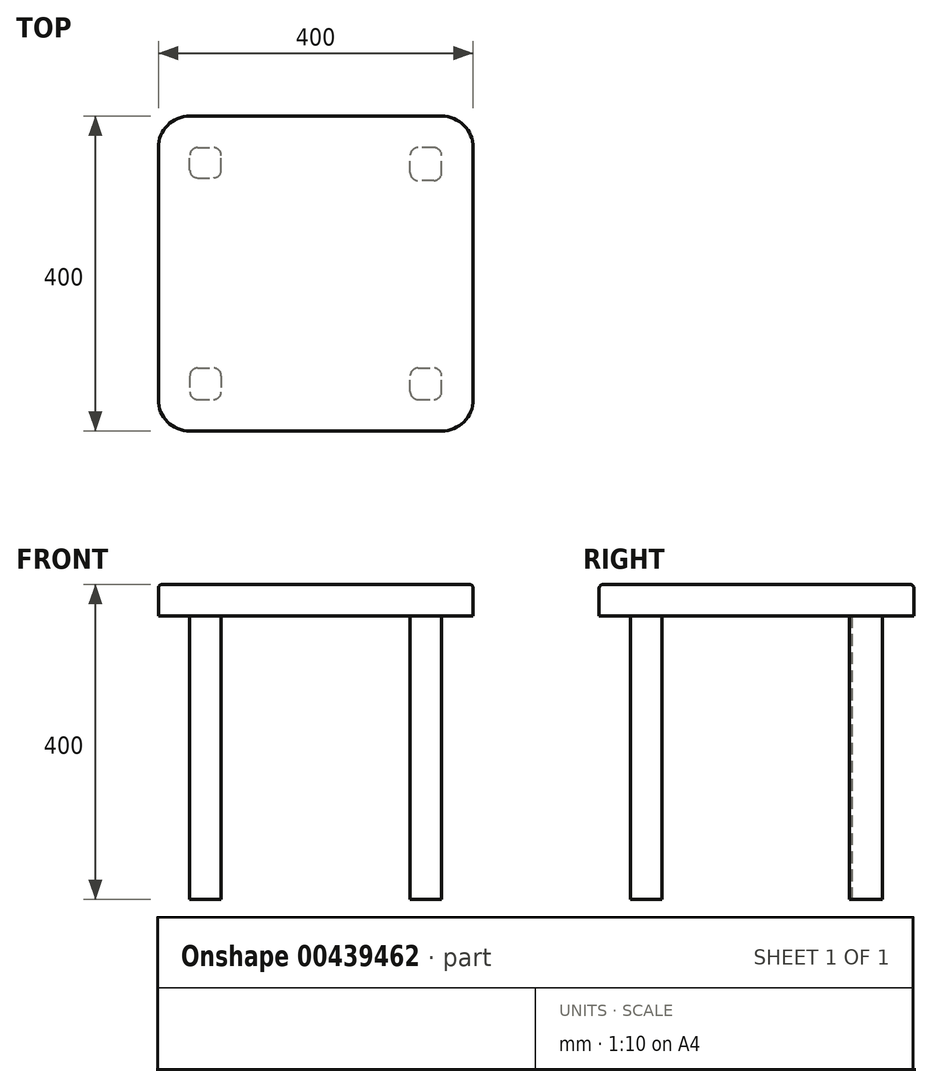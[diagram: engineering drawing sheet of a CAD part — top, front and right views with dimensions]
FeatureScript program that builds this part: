
annotation { "Feature Type Name" : "Feature", "Feature Type Description" : "" }
export const myFeature = defineFeature(function(context is Context, id is Id, definition is map)
    precondition{}
    {
        {
            var Q0;
            Q0=qCreatedBy(makeId("Top.planeOp"),FACE);
            var sketch = newSketch(context, id + "F0", { "sketchPlane" : qUnion([Q0])});
            skLineSegment(sketch, "E0.bottom", {"start": v(-145.08, 267.03) * mm, "end": v(174.92, 267.03) * mm});
            skLineSegment(sketch, "E0.top", {"start": v(-145.08, -132.97) * mm, "end": v(174.92, -132.97) * mm});
            skLineSegment(sketch, "E0.left", {"start": v(-185.08, 227.03) * mm, "end": v(-185.08, -92.97) * mm});
            skLineSegment(sketch, "E0.right", {"start": v(214.92, 227.03) * mm, "end": v(214.92, -92.97) * mm});
            skPoint(sketch, "E1.visualSharp", {"position": v(-185.08, 267.03) * mm});
            skArc(sketch, "E1.filletArc", {"start": v(-145.08, 267.03) * mm, "mid": v(-173.36, 255.31) * mm, "end": v(-185.08, 227.03) * mm});
            skPoint(sketch, "E2.visualSharp", {"position": v(-185.08, -132.97) * mm});
            skArc(sketch, "E2.filletArc", {"start": v(-185.08, -92.97) * mm, "mid": v(-173.36, -121.26) * mm, "end": v(-145.08, -132.97) * mm});
            skPoint(sketch, "E3.visualSharp", {"position": v(214.92, -132.97) * mm});
            skArc(sketch, "E3.filletArc", {"start": v(174.92, -132.97) * mm, "mid": v(203.2, -121.26) * mm, "end": v(214.92, -92.97) * mm});
            skPoint(sketch, "E4.visualSharp", {"position": v(214.92, 267.03) * mm});
            skArc(sketch, "E4.filletArc", {"start": v(214.92, 227.03) * mm, "mid": v(203.2, 255.31) * mm, "end": v(174.92, 267.03) * mm});
            skSolve(sketch);
        }
        {
            var Q0;
            Q0 = qSketchRegion(id + "F0", true);
            extrude(context, id + "F1", {"entities" : qUnion([Q0]), "depth" : 40 * mm});
        }
        {
            var Q0;
            Q0=makeQuery(id+"F1.opExtrude","CAP_FACE",FACE,{"disambiguationData":[OSD([sQuery(id+"F0.wireOp",EDGE,"E0.bottom"),sQuery(id+"F0.wireOp",EDGE,"E0.top"),sQuery(id+"F0.wireOp",EDGE,"E0.left"),sQuery(id+"F0.wireOp",EDGE,"E0.right"),sQuery(id+"F0.wireOp",EDGE,"E1.filletArc"),sQuery(id+"F0.wireOp",EDGE,"E2.filletArc"),sQuery(id+"F0.wireOp",EDGE,"E3.filletArc"),sQuery(id+"F0.wireOp",EDGE,"E4.filletArc")])],"isStart":true});
            var sketch = newSketch(context, id + "F2", { "sketchPlane" : qUnion([Q0])});
            skLineSegment(sketch, "E5.bottom", {"start": v(-135.08, 52.97) * mm, "end": v(-115.08, 52.97) * mm});
            skLineSegment(sketch, "E5.top", {"start": v(-135.08, 92.97) * mm, "end": v(-115.08, 92.97) * mm});
            skLineSegment(sketch, "E5.left", {"start": v(-145.08, 62.97) * mm, "end": v(-145.08, 82.97) * mm});
            skLineSegment(sketch, "E5.right", {"start": v(-105.08, 62.97) * mm, "end": v(-105.08, 82.97) * mm});
            skPoint(sketch, "E6.visualSharp", {"position": v(-145.08, 92.97) * mm});
            skArc(sketch, "E6.filletArc", {"start": v(-135.08, 92.97) * mm, "mid": v(-142.15, 90.04) * mm, "end": v(-145.08, 82.97) * mm});
            skPoint(sketch, "E7.visualSharp", {"position": v(-105.08, 92.97) * mm});
            skArc(sketch, "E7.filletArc", {"start": v(-105.08, 82.97) * mm, "mid": v(-108, 90.04) * mm, "end": v(-115.08, 92.97) * mm});
            skPoint(sketch, "E8.visualSharp", {"position": v(-105.08, 52.97) * mm});
            skArc(sketch, "E8.filletArc", {"start": v(-115.08, 52.97) * mm, "mid": v(-108, 55.9) * mm, "end": v(-105.08, 62.97) * mm});
            skPoint(sketch, "E9.visualSharp", {"position": v(-145.08, 52.97) * mm});
            skArc(sketch, "E9.filletArc", {"start": v(-145.08, 62.97) * mm, "mid": v(-142.15, 55.9) * mm, "end": v(-135.08, 52.97) * mm});
            skLineSegment(sketch, "E10.bottom", {"start": v(-135.08, -188.62) * mm, "end": v(-115.08, -188.62) * mm});
            skLineSegment(sketch, "E10.top", {"start": v(-135.08, -227.03) * mm, "end": v(-115.08, -227.03) * mm});
            skLineSegment(sketch, "E10.left", {"start": v(-145.08, -198.62) * mm, "end": v(-145.08, -217.03) * mm});
            skLineSegment(sketch, "E10.right", {"start": v(-105.08, -198.62) * mm, "end": v(-105.08, -217.03) * mm});
            skLineSegment(sketch, "E11.bottom", {"start": v(164.92, -185.22) * mm, "end": v(144.92, -185.22) * mm});
            skLineSegment(sketch, "E11.top", {"start": v(164.92, -227.03) * mm, "end": v(144.92, -227.03) * mm});
            skLineSegment(sketch, "E11.left", {"start": v(174.92, -195.22) * mm, "end": v(174.92, -217.03) * mm});
            skLineSegment(sketch, "E11.right", {"start": v(134.92, -195.22) * mm, "end": v(134.92, -217.03) * mm});
            skLineSegment(sketch, "E12.bottom", {"start": v(144.92, 92.97) * mm, "end": v(164.92, 92.97) * mm});
            skLineSegment(sketch, "E12.top", {"start": v(144.92, 53.04) * mm, "end": v(164.92, 53.04) * mm});
            skLineSegment(sketch, "E12.left", {"start": v(134.92, 82.97) * mm, "end": v(134.92, 63.04) * mm});
            skLineSegment(sketch, "E12.right", {"start": v(174.92, 82.97) * mm, "end": v(174.92, 63.04) * mm});
            skPoint(sketch, "E13.visualSharp", {"position": v(-105.08, -188.62) * mm});
            skArc(sketch, "E13.filletArc", {"start": v(-105.08, -198.62) * mm, "mid": v(-108, -191.55) * mm, "end": v(-115.08, -188.62) * mm});
            skPoint(sketch, "E14.visualSharp", {"position": v(-105.08, -227.03) * mm});
            skArc(sketch, "E14.filletArc", {"start": v(-115.08, -227.03) * mm, "mid": v(-108, -224.1) * mm, "end": v(-105.08, -217.03) * mm});
            skPoint(sketch, "E15.visualSharp", {"position": v(-145.08, -227.03) * mm});
            skArc(sketch, "E15.filletArc", {"start": v(-145.08, -217.03) * mm, "mid": v(-142.15, -224.1) * mm, "end": v(-135.08, -227.03) * mm});
            skPoint(sketch, "E16.visualSharp", {"position": v(-145.08, -188.62) * mm});
            skArc(sketch, "E16.filletArc", {"start": v(-135.08, -188.62) * mm, "mid": v(-142.15, -191.55) * mm, "end": v(-145.08, -198.62) * mm});
            skPoint(sketch, "E17.visualSharp", {"position": v(134.92, -185.22) * mm});
            skArc(sketch, "E17.filletArc", {"start": v(144.92, -185.22) * mm, "mid": v(137.85, -188.15) * mm, "end": v(134.92, -195.22) * mm});
            skPoint(sketch, "E18.visualSharp", {"position": v(174.92, -185.22) * mm});
            skArc(sketch, "E18.filletArc", {"start": v(174.92, -195.22) * mm, "mid": v(172, -188.15) * mm, "end": v(164.92, -185.22) * mm});
            skPoint(sketch, "E19.visualSharp", {"position": v(134.92, -227.03) * mm});
            skArc(sketch, "E19.filletArc", {"start": v(134.92, -217.03) * mm, "mid": v(137.85, -224.1) * mm, "end": v(144.92, -227.03) * mm});
            skPoint(sketch, "E20.visualSharp", {"position": v(174.92, -227.03) * mm});
            skArc(sketch, "E20.filletArc", {"start": v(164.92, -227.03) * mm, "mid": v(172, -224.1) * mm, "end": v(174.92, -217.03) * mm});
            skPoint(sketch, "E21.visualSharp", {"position": v(134.92, 92.97) * mm});
            skArc(sketch, "E21.filletArc", {"start": v(144.92, 92.97) * mm, "mid": v(137.85, 90.04) * mm, "end": v(134.92, 82.97) * mm});
            skPoint(sketch, "E22.visualSharp", {"position": v(134.92, 53.04) * mm});
            skArc(sketch, "E22.filletArc", {"start": v(134.92, 63.04) * mm, "mid": v(137.85, 55.97) * mm, "end": v(144.92, 53.04) * mm});
            skPoint(sketch, "E23.visualSharp", {"position": v(174.92, 53.04) * mm});
            skArc(sketch, "E23.filletArc", {"start": v(164.92, 53.04) * mm, "mid": v(172, 55.97) * mm, "end": v(174.92, 63.04) * mm});
            skPoint(sketch, "E24.visualSharp", {"position": v(174.92, 92.97) * mm});
            skArc(sketch, "E24.filletArc", {"start": v(174.92, 82.97) * mm, "mid": v(172, 90.04) * mm, "end": v(164.92, 92.97) * mm});
            skSolve(sketch);
        }
        {
            var Q0;
            Q0 = qSketchRegion(id + "F2", true);
            extrude(context, id + "F3", {"entities" : qUnion([Q0]), "operationType" : NewBodyOperationType.ADD, "depth" : 360 * mm});
        }
        {
            var Q0;
            Q0=makeQuery(id+"F1.opExtrude","CAP_EDGE",EDGE,{"disambiguationData":[OSD([sQuery(id+"F0.wireOp",EDGE,"E0.right")])],"isStart":false});
            var Q1;
            Q1=makeQuery(id+"F1.opExtrude","CAP_EDGE",EDGE,{"disambiguationData":[OSD([sQuery(id+"F0.wireOp",EDGE,"E4.filletArc")])],"isStart":false});
            var Q2;
            Q2=makeQuery(id+"F1.opExtrude","CAP_EDGE",EDGE,{"disambiguationData":[OSD([sQuery(id+"F0.wireOp",EDGE,"E0.bottom")])],"isStart":false});
            var Q3;
            Q3=makeQuery(id+"F1.opExtrude","CAP_FACE",FACE,{"disambiguationData":[OSD([sQuery(id+"F0.wireOp",EDGE,"E0.bottom"),sQuery(id+"F0.wireOp",EDGE,"E0.top"),sQuery(id+"F0.wireOp",EDGE,"E0.left"),sQuery(id+"F0.wireOp",EDGE,"E0.right"),sQuery(id+"F0.wireOp",EDGE,"E1.filletArc"),sQuery(id+"F0.wireOp",EDGE,"E2.filletArc"),sQuery(id+"F0.wireOp",EDGE,"E3.filletArc"),sQuery(id+"F0.wireOp",EDGE,"E4.filletArc")])],"isStart":false});
            fillet(context, id + "F4", {"entities" : qUnion([Q0, Q1, Q2, Q3]), "radius" : 5 * mm, "tangentPropagation" : true, "allowEdgeOverflow" : false});
        }
    });
